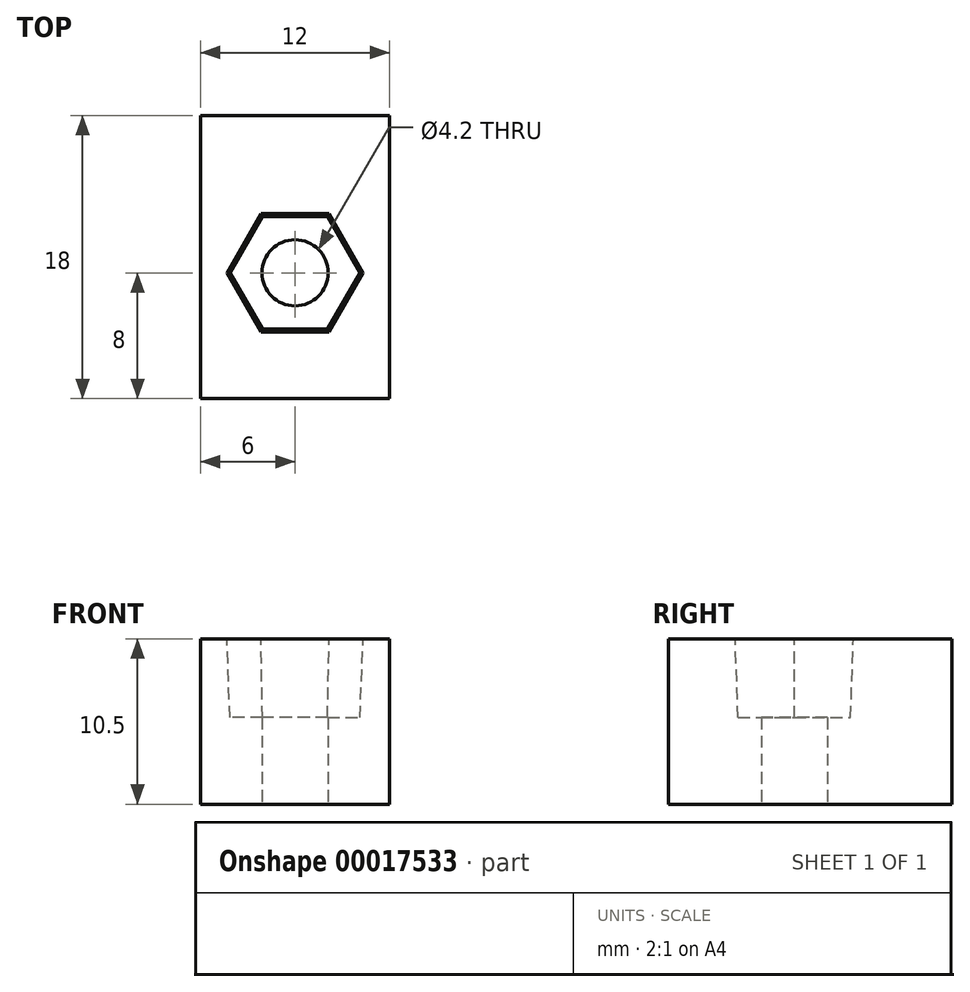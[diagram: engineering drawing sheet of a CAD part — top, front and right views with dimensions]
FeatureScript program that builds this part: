
annotation { "Feature Type Name" : "Feature", "Feature Type Description" : "" }
export const myFeature = defineFeature(function(context is Context, id is Id, definition is map)
    precondition{}
    {
        {
            var Q0;
            Q0=qCreatedBy(makeId("Top.planeOp"),FACE);
            var sketch = newSketch(context, id + "F0", { "sketchPlane" : qUnion([Q0])});
            skLineSegment(sketch, "E0.bottom", {"start": v(6, -8) * mm, "end": v(-6, -8) * mm});
            skLineSegment(sketch, "E0.top", {"start": v(6, 10) * mm, "end": v(-6, 10) * mm});
            skLineSegment(sketch, "E0.left", {"start": v(6, -8) * mm, "end": v(6, 10) * mm});
            skLineSegment(sketch, "E0.right", {"start": v(-6, -8) * mm, "end": v(-6, 10) * mm});
            skPoint(sketch, "E0.middle", {"position": v(0, 1) * mm});
            skCircle(sketch, "E1", {"center": v(0, 0) * mm, "radius": 2.1 * mm});
            skSolve(sketch);
        }
        {
            var Q0;
            Q0 = qSketchRegion(id + "F0", true);
            extrude(context, id + "F1", {"entities" : qUnion([Q0]), "depth" : 10.5 * mm, "offsetDistance" : 25 * mm});
        }
        {
            var Q0;
            Q0=makeQuery(id+"F1.opExtrude","CAP_FACE",FACE,{"disambiguationData":[OSD([sQuery(id+"F0.wireOp",EDGE,"E0.bottom"),sQuery(id+"F0.wireOp",EDGE,"E0.top"),sQuery(id+"F0.wireOp",EDGE,"E0.left"),sQuery(id+"F0.wireOp",EDGE,"E0.right"),sQuery(id+"F0.wireOp",EDGE,"E1")])],"isStart":false});
            var sketch = newSketch(context, id + "F2", { "sketchPlane" : qUnion([Q0])});
            skCircle(sketch, "E2.cCircle", {"center": v(0, 0) * mm, "radius": 3.75 * mm, "construction": true});
            skLineSegment(sketch, "E2.0", {"start": v(4.33, 0) * mm, "end": v(2.17, -3.75) * mm});
            skLineSegment(sketch, "E2.1", {"start": v(2.17, -3.75) * mm, "end": v(-2.17, -3.75) * mm});
            skLineSegment(sketch, "E2.2", {"start": v(-2.17, -3.75) * mm, "end": v(-4.33, 0) * mm});
            skLineSegment(sketch, "E2.3", {"start": v(-4.33, 0) * mm, "end": v(-2.17, 3.75) * mm});
            skLineSegment(sketch, "E2.4", {"start": v(-2.17, 3.75) * mm, "end": v(2.17, 3.75) * mm});
            skLineSegment(sketch, "E2.5", {"start": v(2.17, 3.75) * mm, "end": v(4.33, 0) * mm});
            skPoint(sketch, "E2.0.midPoint", {"position": v(3.25, -1.88) * mm});
            skSolve(sketch);
        }
        {
            var Q0;
            Q0 = qSketchRegion(id + "F2", true);
            extrude(context, id + "F3", {"entities" : qUnion([Q0]), "operationType" : NewBodyOperationType.REMOVE, "oppositeDirection" : true, "depth" : 5 * mm, "offsetDistance" : 25 * mm, "hasDraft" : true, "draftAngle" : 2 * degree, "draftPullDirection" : true});
        }
    });
